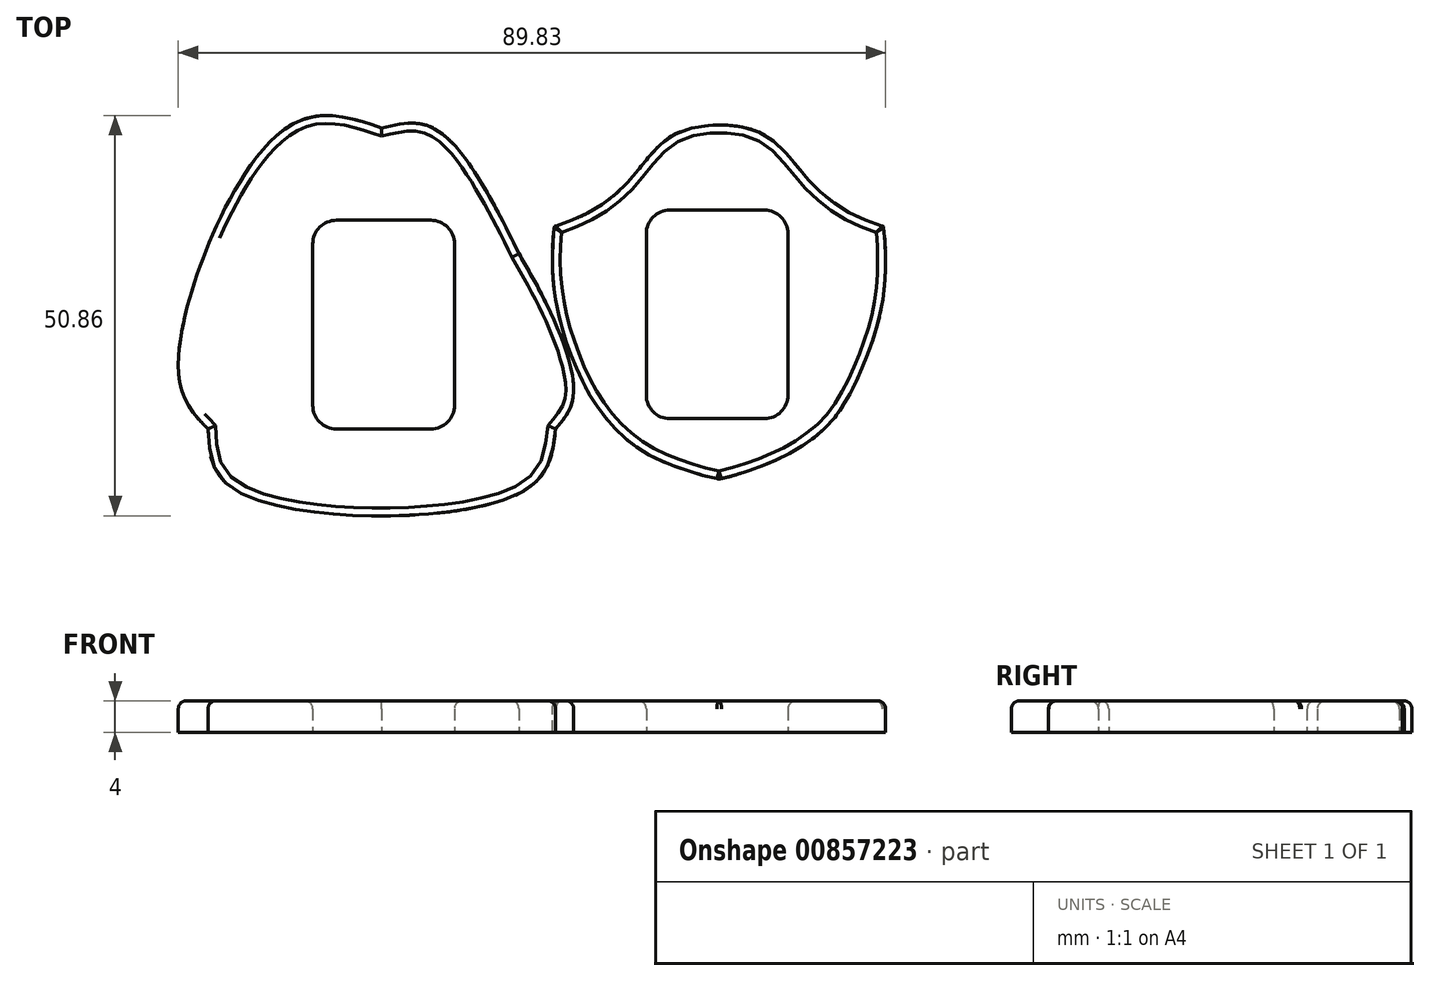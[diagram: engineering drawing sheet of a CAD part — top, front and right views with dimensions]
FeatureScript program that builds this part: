
annotation { "Feature Type Name" : "Feature", "Feature Type Description" : "" }
export const myFeature = defineFeature(function(context is Context, id is Id, definition is map)
    precondition{}
    {
        {
            var Q0;
            Q0=qCreatedBy(makeId("Top.planeOp"),FACE);
            var sketch = newSketch(context, id + "F0", { "sketchPlane" : qUnion([Q0])});
            skFitSpline(sketch, "E0", {"points": [v(44.02, -22.15) * mm, v(44.02, -22.15) * mm, v(44.02, -22.15) * mm, v(44.02, -22.15) * mm]});
            skFitSpline(sketch, "E1", {"points": [v(44.02, -22.15) * mm, v(44.02, -22.15) * mm, v(44.02, -22.15) * mm, v(44.02, -22.15) * mm]});
            skFitSpline(sketch, "E2", {"points": [v(-20.6, -16.1) * mm, v(-24.38, -8.15) * mm, v(-11.05, 21.85) * mm, v(1.46, 22.11) * mm]});
            skFitSpline(sketch, "E3", {"points": [v(1.46, 22.11) * mm, v(7.72, 22.25) * mm, v(14.36, 14.73) * mm, v(18.87, 6.16) * mm]});
            skFitSpline(sketch, "E4", {"points": [v(18.87, 6.16) * mm, v(23.4, -2.41) * mm, v(25.78, -12.03) * mm, v(23.53, -16.1) * mm]});
            skFitSpline(sketch, "E5", {"points": [v(23.53, -16.1) * mm, v(19.03, -24.25) * mm, v(-16.83, -24.07) * mm, v(-20.6, -16.1) * mm]});
            skFitSpline(sketch, "E6", {"points": [v(-20.6, -0.02) * mm, v(-20.6, 12.2) * mm, v(-30.5, 22.12) * mm, v(-42.73, 22.12) * mm, v(-54.96, 22.12) * mm, v(-64.86, 12.2) * mm, v(-64.86, -0.02) * mm, v(-64.86, -12.24) * mm, v(-54.96, -22.15) * mm, v(-42.73, -22.15) * mm, v(-30.5, -22.15) * mm, v(-20.6, -12.24) * mm, v(-20.6, -0.02) * mm]});
            skLineSegment(sketch, "E7.bottom", {"start": v(-33.47, -13.25) * mm, "end": v(-51.47, -13.25) * mm});
            skLineSegment(sketch, "E7.top", {"start": v(-33.47, 13.25) * mm, "end": v(-51.47, 13.25) * mm});
            skLineSegment(sketch, "E7.left", {"start": v(-33.47, -13.25) * mm, "end": v(-33.47, 13.25) * mm});
            skLineSegment(sketch, "E7.right", {"start": v(-51.47, -13.25) * mm, "end": v(-51.47, 13.25) * mm});
            skPoint(sketch, "E7.middle", {"position": v(-42.47, 0) * mm});
            skLineSegment(sketch, "E8.bottom", {"start": v(10.7, -16.1) * mm, "end": v(-7.3, -16.1) * mm});
            skLineSegment(sketch, "E8.top", {"start": v(10.7, 10.4) * mm, "end": v(-7.3, 10.4) * mm});
            skLineSegment(sketch, "E8.left", {"start": v(10.7, -16.1) * mm, "end": v(10.7, 10.4) * mm});
            skLineSegment(sketch, "E8.right", {"start": v(-7.3, -16.1) * mm, "end": v(-7.3, 10.4) * mm});
            skLineSegment(sketch, "E9.bottom", {"start": v(53.06, -14.8) * mm, "end": v(35.06, -14.8) * mm});
            skLineSegment(sketch, "E9.top", {"start": v(53.06, 11.7) * mm, "end": v(35.06, 11.7) * mm});
            skLineSegment(sketch, "E9.left", {"start": v(53.06, -14.8) * mm, "end": v(53.06, 11.7) * mm});
            skLineSegment(sketch, "E9.right", {"start": v(35.06, -14.8) * mm, "end": v(35.06, 11.7) * mm});
            skPoint(sketch, "E9.middle", {"position": v(44.06, -1.56) * mm});
            skSolve(sketch);
        }
        {
            var Q0;
            Q0=qCreatedBy(makeId("Top.planeOp"),FACE);
            var sketch = newSketch(context, id + "F1", { "sketchPlane" : qUnion([Q0])});
            skFitSpline(sketch, "E10", {"points": [v(23.41, 9.58) * mm, v(23.3, 2.1) * mm, v(26.28, -8.6) * mm, v(28.9, -13.36) * mm, v(32, -16.94) * mm, v(37.4, -20.37) * mm, v(44.14, -22.45) * mm, v(44.32, -22.45) * mm, v(44.46, -22.45) * mm, v(50.56, -20.5) * mm, v(56.72, -16.93) * mm, v(59.7, -13.7) * mm, v(62.54, -8.21) * mm, v(65.31, 2.06) * mm, v(65.16, 9.62) * mm, v(65.04, 9.68) * mm, v(61.76, 10.92) * mm, v(58.59, 12.86) * mm, v(55.94, 15.18) * mm, v(52.76, 18.96) * mm, v(49.3, 21.62) * mm, v(44.27, 22.5) * mm, v(39.18, 21.56) * mm, v(35.61, 18.71) * mm, v(32.49, 14.97) * mm, v(29.8, 12.67) * mm, v(26.52, 10.77) * mm, v(23.54, 9.67) * mm, v(23.41, 9.58) * mm]});
            skLineSegment(sketch, "E11.0.0", {"start": v(53.06, -14.8) * mm, "end": v(53.06, 11.7) * mm});
            skLineSegment(sketch, "E11.0.1", {"start": v(53.06, 11.7) * mm, "end": v(35.06, 11.7) * mm});
            skLineSegment(sketch, "E11.0.2", {"start": v(35.06, 11.7) * mm, "end": v(35.06, -14.8) * mm});
            skLineSegment(sketch, "E11.0.3", {"start": v(35.06, -14.8) * mm, "end": v(53.06, -14.8) * mm});
            skSolve(sketch);
        }
        {
            var Q0;
            Q0=makeQuery(id+"F0.imprint","IMPRINT",FACE,{"disambiguationData":[TD([[makeQuery(id+"F0.imprint","IMPRINT",EDGE,{"derivedFrom":sQuery(id+"F0.wireOp",EDGE,"E6")}),1.0]])]});
            var Q1;
            Q1=makeQuery(id+"F0.imprint","IMPRINT",FACE,{"disambiguationData":[TD([[makeQuery(id+"F0.imprint","IMPRINT",EDGE,{"derivedFrom":sQuery(id+"F0.wireOp",EDGE,"E2")}),-1.0]])]});
            var Q2;
            Q2=makeQuery(id+"F1.imprint","IMPRINT",FACE,{"disambiguationData":[TD([[makeQuery(id+"F1.imprint","IMPRINT",EDGE,{"derivedFrom":sQuery(id+"F1.wireOp",EDGE,"E10")}),1.0]])]});
            extrude(context, id + "F2", {"entities" : qUnion([Q0, Q1, Q2]), "depth" : 4 * mm, "offsetDistance" : 25 * mm});
        }
        {
            var Q0;
            Q0=makeQuery(id+"F2.opExtrude","SWEPT_EDGE",EDGE,{"disambiguationData":[OSD([sQuery(id+"F0.wireOp",EDGE,"E7.top"),sQuery(id+"F0.wireOp",EDGE,"E7.right")])]});
            var Q1;
            Q1=makeQuery(id+"F2.opExtrude","SWEPT_EDGE",EDGE,{"disambiguationData":[OSD([sQuery(id+"F0.wireOp",EDGE,"E7.top"),sQuery(id+"F0.wireOp",EDGE,"E7.left")])]});
            var Q2;
            Q2=makeQuery(id+"F2.opExtrude","SWEPT_EDGE",EDGE,{"disambiguationData":[OSD([sQuery(id+"F0.wireOp",EDGE,"E7.bottom"),sQuery(id+"F0.wireOp",EDGE,"E7.right")])]});
            var Q3;
            Q3=makeQuery(id+"F2.opExtrude","SWEPT_EDGE",EDGE,{"disambiguationData":[OSD([sQuery(id+"F0.wireOp",EDGE,"E7.bottom"),sQuery(id+"F0.wireOp",EDGE,"E7.left")])]});
            var Q4;
            Q4=makeQuery(id+"F2.opExtrude","SWEPT_EDGE",EDGE,{"disambiguationData":[OSD([sQuery(id+"F0.wireOp",EDGE,"E8.bottom"),sQuery(id+"F0.wireOp",EDGE,"E8.right")])]});
            var Q5;
            Q5=makeQuery(id+"F2.opExtrude","SWEPT_EDGE",EDGE,{"disambiguationData":[OSD([sQuery(id+"F0.wireOp",EDGE,"E8.bottom"),sQuery(id+"F0.wireOp",EDGE,"E8.left")])]});
            var Q6;
            Q6=makeQuery(id+"F2.opExtrude","SWEPT_EDGE",EDGE,{"disambiguationData":[OSD([sQuery(id+"F0.wireOp",EDGE,"E8.top"),sQuery(id+"F0.wireOp",EDGE,"E8.right")])]});
            var Q7;
            Q7=makeQuery(id+"F2.opExtrude","SWEPT_EDGE",EDGE,{"disambiguationData":[OSD([sQuery(id+"F0.wireOp",EDGE,"E8.top"),sQuery(id+"F0.wireOp",EDGE,"E8.left")])]});
            var Q8;
            Q8=makeQuery(id+"F2.opExtrude","SWEPT_EDGE",EDGE,{"disambiguationData":[OSD([sQuery(id+"F1.wireOp",EDGE,"E11.0.0"),sQuery(id+"F1.wireOp",EDGE,"E11.0.1")])]});
            var Q9;
            Q9=makeQuery(id+"F2.opExtrude","SWEPT_EDGE",EDGE,{"disambiguationData":[OSD([sQuery(id+"F1.wireOp",EDGE,"E11.0.1"),sQuery(id+"F1.wireOp",EDGE,"E11.0.2")])]});
            var Q10;
            Q10=makeQuery(id+"F2.opExtrude","SWEPT_EDGE",EDGE,{"disambiguationData":[OSD([sQuery(id+"F1.wireOp",EDGE,"E11.0.2"),sQuery(id+"F1.wireOp",EDGE,"E11.0.3")])]});
            var Q11;
            Q11=makeQuery(id+"F2.opExtrude","SWEPT_EDGE",EDGE,{"disambiguationData":[OSD([sQuery(id+"F1.wireOp",EDGE,"E11.0.0"),sQuery(id+"F1.wireOp",EDGE,"E11.0.3")])]});
            fillet(context, id + "F3", {"entities" : qUnion([Q0, Q1, Q2, Q3, Q4, Q5, Q6, Q7, Q8, Q9, Q10, Q11]), "radius" : 3 * mm, "tangentPropagation" : true, "allowEdgeOverflow" : false});
        }
        {
            var Q0;
            Q0=makeQuery(id+"F2.opExtrude","CAP_FACE",FACE,{"disambiguationData":[OSD([sQuery(id+"F1.wireOp",EDGE,"E10"),sQuery(id+"F1.wireOp",EDGE,"E11.0.0"),sQuery(id+"F1.wireOp",EDGE,"E11.0.1"),sQuery(id+"F1.wireOp",EDGE,"E11.0.2"),sQuery(id+"F1.wireOp",EDGE,"E11.0.3")])],"isStart":false});
            var Q1;
            Q1=makeQuery(id+"F2.opExtrude","CAP_FACE",FACE,{"disambiguationData":[OSD([sQuery(id+"F0.wireOp",EDGE,"E2"),sQuery(id+"F0.wireOp",EDGE,"E3"),sQuery(id+"F0.wireOp",EDGE,"E4"),sQuery(id+"F0.wireOp",EDGE,"E5"),sQuery(id+"F0.wireOp",EDGE,"E8.bottom"),sQuery(id+"F0.wireOp",EDGE,"E8.top"),sQuery(id+"F0.wireOp",EDGE,"E8.left"),sQuery(id+"F0.wireOp",EDGE,"E8.right")])],"isStart":false});
            var Q2;
            Q2=makeQuery(id+"F2.opExtrude","CAP_FACE",FACE,{"disambiguationData":[OSD([sQuery(id+"F0.wireOp",EDGE,"E6"),sQuery(id+"F0.wireOp",EDGE,"E7.bottom"),sQuery(id+"F0.wireOp",EDGE,"E7.top"),sQuery(id+"F0.wireOp",EDGE,"E7.left"),sQuery(id+"F0.wireOp",EDGE,"E7.right")])],"isStart":false});
            fillet(context, id + "F4", {"entities" : qUnion([Q0, Q1, Q2]), "radius" : 1 * mm, "tangentPropagation" : true, "allowEdgeOverflow" : false});
        }
    });
